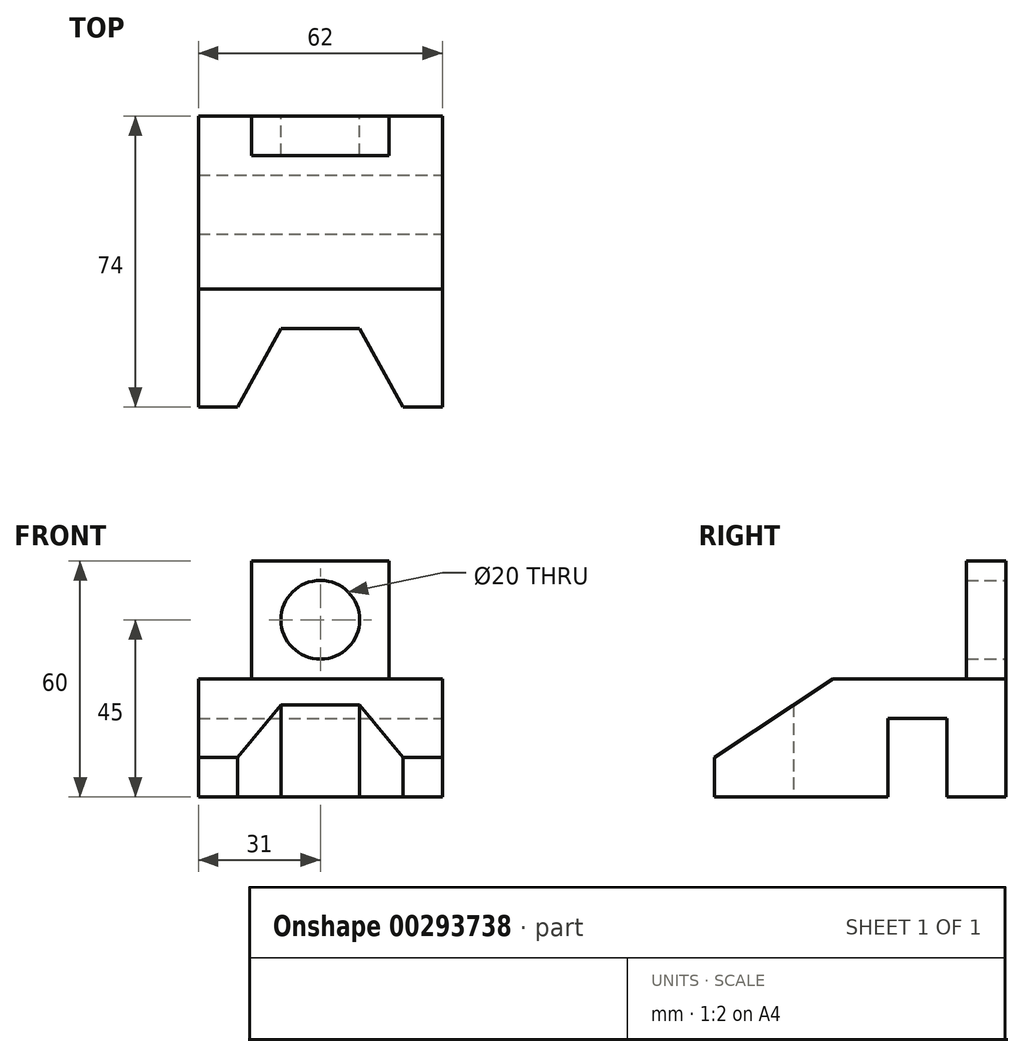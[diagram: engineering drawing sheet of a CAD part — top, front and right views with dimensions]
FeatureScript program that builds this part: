
annotation { "Feature Type Name" : "Feature", "Feature Type Description" : "" }
export const myFeature = defineFeature(function(context is Context, id is Id, definition is map)
    precondition{}
    {
        {
            var Q0;
            Q0=qCreatedBy(makeId("Top.planeOp"),FACE);
            var sketch = newSketch(context, id + "F0", { "sketchPlane" : qUnion([Q0])});
            skLineSegment(sketch, "E0.bottom", {"start": v(31, -37) * mm, "end": v(21, -37) * mm});
            skLineSegment(sketch, "E0.top", {"start": v(31, 37) * mm, "end": v(-31, 37) * mm});
            skLineSegment(sketch, "E0.left", {"start": v(31, -37) * mm, "end": v(31, 37) * mm});
            skLineSegment(sketch, "E0.right", {"start": v(-31, -37) * mm, "end": v(-31, 37) * mm});
            skPoint(sketch, "E0.middle", {"position": v(0, 0) * mm});
            skLineSegment(sketch, "E1.0", {"start": v(10, -17) * mm, "end": v(0, -17) * mm});
            skPoint(sketch, "E2.endSnap0", {"position": v(0, -17) * mm});
            skLineSegment(sketch, "E3", {"start": v(10, -17) * mm, "end": v(21, -37) * mm});
            skPoint(sketch, "E4.orphan", {"position": v(31, -17) * mm});
            skPoint(sketch, "E5.orphan", {"position": v(-31, -17) * mm});
            skPoint(sketch, "E2.end.orphan", {"position": v(0, -28.4) * mm});
            skLineSegment(sketch, "E6.MirrorCS", {"start": v(-10, -17) * mm, "end": v(-21, -37) * mm});
            skLineSegment(sketch, "E7.MirrorCS", {"start": v(-10, -17) * mm, "end": v(0, -17) * mm});
            skLineSegment(sketch, "E8.trimOffspring", {"start": v(-21, -37) * mm, "end": v(-31, -37) * mm});
            skSolve(sketch);
        }
        {
            var Q0;
            Q0=makeQuery(id+"F0.imprint","IMPRINT",FACE,{"disambiguationData":[TD([[makeQuery(id+"F0.imprint","IMPRINT",EDGE,{"derivedFrom":sQuery(id+"F0.wireOp",EDGE,"E0.bottom")}),-1.0]])]});
            extrude(context, id + "F1", {"entities" : qUnion([Q0]), "depth" : 30 * mm});
        }
        {
            var Q0;
            Q0=makeQuery(id+"F1.opExtrude","SWEPT_FACE",FACE,{"disambiguationData":[OSD([sQuery(id+"F0.wireOp",EDGE,"E0.left")])]});
            var sketch = newSketch(context, id + "F2", { "sketchPlane" : qUnion([Q0])});
            skLineSegment(sketch, "E9", {"start": v(-7, 30) * mm, "end": v(-37, 10) * mm});
            skPoint(sketch, "E10.start.orphan", {"position": v(-53.66, 0) * mm});
            skLineSegment(sketch, "E11", {"start": v(-37, 10) * mm, "end": v(-44.99, 10) * mm});
            skLineSegment(sketch, "E12", {"start": v(-44.99, 10) * mm, "end": v(-44.99, 33.15) * mm});
            skLineSegment(sketch, "E13", {"start": v(-44.99, 33.15) * mm, "end": v(-7.2, 33.15) * mm});
            skLineSegment(sketch, "E14", {"start": v(-7.2, 33.15) * mm, "end": v(-7, 30) * mm});
            skLineSegment(sketch, "E15", {"start": v(22, 0) * mm, "end": v(22, 20) * mm});
            skLineSegment(sketch, "E16", {"start": v(22, 20) * mm, "end": v(7, 20) * mm});
            skLineSegment(sketch, "E17", {"start": v(7, 20) * mm, "end": v(7, -7.73) * mm});
            skLineSegment(sketch, "E18", {"start": v(22, 0) * mm, "end": v(22, -7.73) * mm});
            skLineSegment(sketch, "E19", {"start": v(22, -7.73) * mm, "end": v(7, -7.73) * mm});
            skSolve(sketch);
        }
        {
            var Q0;
            {var subQ0=sQuery(id+"F2.wireOp",EDGE,"E15");Q0=makeQuery(id+"F2.imprint","IMPRINT",FACE,{"disambiguationData":[TD([[makeQuery(id+"F2.imprint","IMPRINT",EDGE,{"derivedFrom":subQ0}),1.0]])]});}
            var Q1;
            {var subQ0=sQuery(id+"F2.wireOp",EDGE,"E9");Q1=makeQuery(id+"F2.imprint","IMPRINT",FACE,{"disambiguationData":[TD([[makeQuery(id+"F2.imprint","IMPRINT",EDGE,{"derivedFrom":subQ0}),-1.0]])]});}
            extrude(context, id + "F3", {"entities" : qUnion([Q0, Q1]), "operationType" : NewBodyOperationType.REMOVE, "oppositeDirection" : true, "depth" : 84.5 * mm});
        }
        {
            var Q0;
            Q0=makeQuery(id+"F1.opExtrude","CAP_FACE",FACE,{"disambiguationData":[OSD([sQuery(id+"F0.wireOp",EDGE,"E0.bottom"),sQuery(id+"F0.wireOp",EDGE,"E0.top"),sQuery(id+"F0.wireOp",EDGE,"E0.left"),sQuery(id+"F0.wireOp",EDGE,"E0.right"),sQuery(id+"F0.wireOp",EDGE,"E1.0"),sQuery(id+"F0.wireOp",EDGE,"E3"),sQuery(id+"F0.wireOp",EDGE,"E6.MirrorCS"),sQuery(id+"F0.wireOp",EDGE,"E7.MirrorCS"),sQuery(id+"F0.wireOp",EDGE,"E8.trimOffspring")])],"isStart":false});
            var sketch = newSketch(context, id + "F4", { "sketchPlane" : qUnion([Q0])});
            skLineSegment(sketch, "E20.bottom", {"start": v(17.5, 27) * mm, "end": v(-17.5, 27) * mm});
            skLineSegment(sketch, "E20.left", {"start": v(17.5, 27) * mm, "end": v(17.5, 37) * mm});
            skLineSegment(sketch, "E20.right", {"start": v(-17.5, 27) * mm, "end": v(-17.5, 37) * mm});
            skPoint(sketch, "E20.middle", {"position": v(0, 37) * mm});
            skLineSegment(sketch, "E21", {"start": v(-17.5, 37) * mm, "end": v(17.5, 37) * mm});
            skPoint(sketch, "E22.orphan", {"position": v(17.5, 47) * mm});
            skPoint(sketch, "E23.orphan", {"position": v(-17.5, 47) * mm});
            skSolve(sketch);
        }
        {
            var Q0;
            Q0 = qSketchRegion(id + "F4", true);
            extrude(context, id + "F5", {"entities" : qUnion([Q0]), "operationType" : NewBodyOperationType.ADD, "offsetDistance" : 25 * mm, "depth" : 30 * mm});
        }
        {
            var Q0;
            Q0=makeQuery(id+"F5.boolean.opBoolean","MERGE",FACE,{"derivedFrom":[makeQuery(id+"F1.opExtrude","SWEPT_FACE",FACE,{"disambiguationData":[OSD([sQuery(id+"F0.wireOp",EDGE,"E0.top")])]}),makeQuery(id+"F5.opExtrude","SWEPT_FACE",FACE,{"disambiguationData":[OSD([sQuery(id+"F4.wireOp",EDGE,"E21")])]})]});
            var sketch = newSketch(context, id + "F6", { "sketchPlane" : qUnion([Q0])});
            skCircle(sketch, "E24", {"center": v(0, 45) * mm, "radius": 10 * mm});
            skPoint(sketch, "E24.centerSnap0", {"position": v(17.5, 45) * mm});
            skSolve(sketch);
        }
        {
            var Q0;
            Q0 = qSketchRegion(id + "F6", true);
            extrude(context, id + "F7", {"entities" : qUnion([Q0]), "operationType" : NewBodyOperationType.REMOVE, "oppositeDirection" : true, "depth" : 25 * mm});
        }
    });
